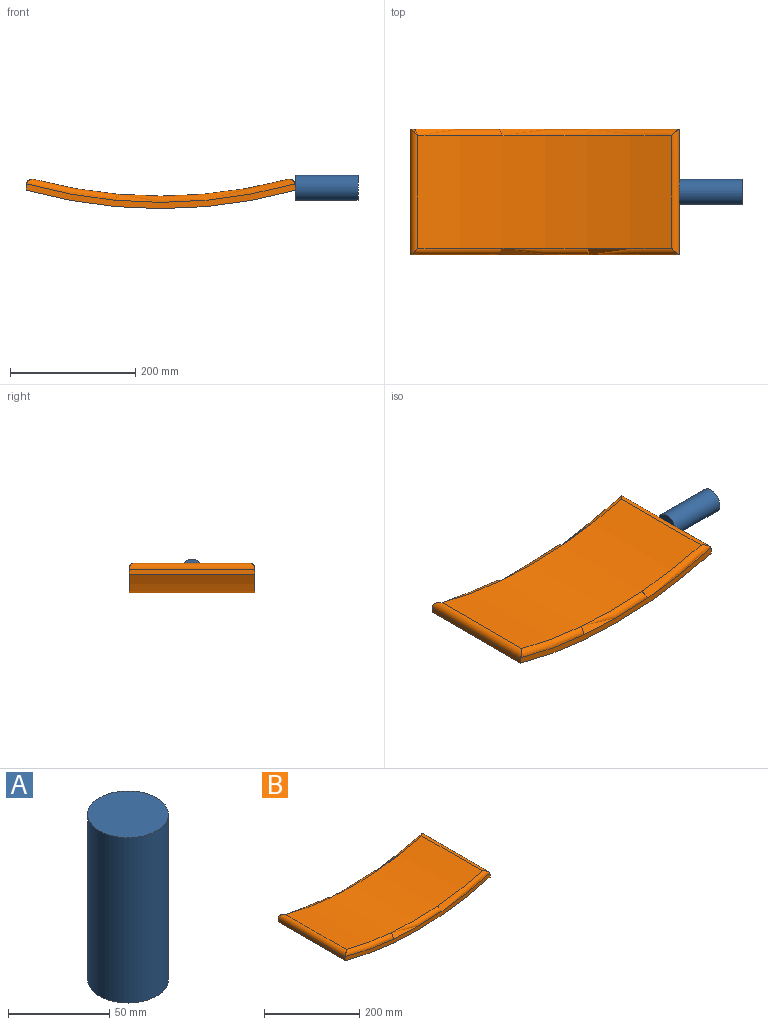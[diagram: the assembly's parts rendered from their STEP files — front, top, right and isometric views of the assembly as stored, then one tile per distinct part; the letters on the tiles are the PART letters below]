
ASSEMBLY  parts=2 mates=1
PART A: 3 faces, bbox 40x40x100 mm
  f0: cylinder r=20mm len=100mm, axis (0,0,-1), area 12566.4mm2, adj f1,f2
  f1: plane 40x40mm, normal (0,0,1), area 1256.6mm2, adj f0
  f2: plane 40x40mm, normal (0,0,-1), area 1256.6mm2, adj f0
PART B: 10 faces, bbox 468.8x200x112.2 mm
  f0: cylinder r=781.56mm len=404.82mm, axis (0,1,0), area 73707.8mm2, adj f6,f7,f8,f9
  f1: plane 200x7.63mm, normal (-1,0,0), area 1526.8mm2, adj f2,f4,f5,f9
  f2: cylinder r=801.56mm len=430mm, axis (0,1,0), area 87066.1mm2, adj f1,f3,f4,f5
  f3: plane 200x7.63mm, normal (1,0,0), area 1526.8mm2, adj f2,f4,f5,f6
  f4: plane 430x39.66mm, normal (0,-1,0), area 4353.3mm2, adj f1,f2,f3,f6,f7,f9
  f5: plane 430x39.66mm, normal (0,1,0), area 4353.3mm2, adj f1,f2,f3,f6,f8,f9
  f6: cylinder r=10mm len=200mm, axis (0,1,0), area 3552mm2, adj f0,f3,f4,f5,f7,f8
  f7: torus R=791.56mm, axis (0,-1,0), area 6661.6mm2, adj f0,f4,f6,f9
  f8: torus R=791.56mm, axis (0,-1,0), area 6661.6mm2, adj f0,f5,f6,f9
  f9: cylinder r=10mm len=200mm, axis (0,1,0), area 3552mm2, adj f0,f1,f4,f5,f7,f8
PLACE A rot(axis=(0.71,0,-0.71),180deg) t=(82.65,-103.09,56.27)mm
PLACE B t=(-84.29,-3.09,18.15)mm
MATE fastened A.f0 <-> B.f3  axis (-1,0,0) through (-17.35,-103.09,56.27)mm
